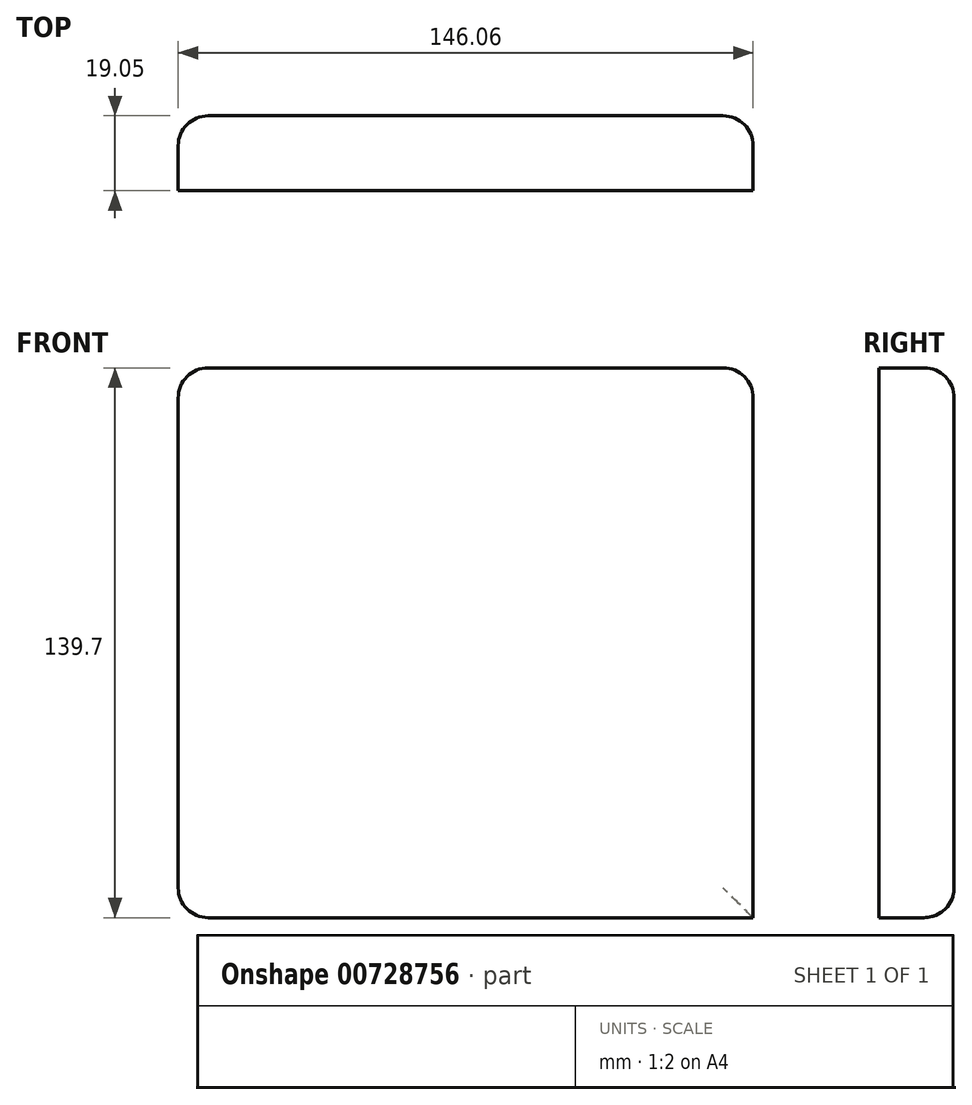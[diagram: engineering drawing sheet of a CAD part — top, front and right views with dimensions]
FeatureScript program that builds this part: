
annotation { "Feature Type Name" : "Feature", "Feature Type Description" : "" }
export const myFeature = defineFeature(function(context is Context, id is Id, definition is map)
    precondition{}
    {
        {
            var Q0;
            Q0=qCreatedBy(makeId("Front.planeOp"),FACE);
            var sketch = newSketch(context, id + "F0", { "sketchPlane" : qUnion([Q0])});
            skLineSegment(sketch, "E0.bottom", {"start": v(73.03, -69.85) * mm, "end": v(-73.03, -69.85) * mm});
            skLineSegment(sketch, "E0.top", {"start": v(73.03, 69.85) * mm, "end": v(-73.03, 69.85) * mm});
            skLineSegment(sketch, "E0.left", {"start": v(73.03, -69.85) * mm, "end": v(73.03, 69.85) * mm});
            skLineSegment(sketch, "E0.right", {"start": v(-73.03, -69.85) * mm, "end": v(-73.03, 69.85) * mm});
            skPoint(sketch, "E0.middle", {"position": v(0, 0) * mm});
            skSolve(sketch);
        }
        {
            var Q0;
            Q0=qSketchRegion(id+"F0",true);
            extrude(context, id + "F1", {"entities" : qUnion([Q0]), "depth" : 19.05 * mm, "offsetDistance" : 25.4 * mm});
        }
        {
            var Q0;
            Q0=makeQuery(id+"F1.opExtrude","CAP_EDGE",EDGE,{"disambiguationData":[OSD([sQuery(id+"F0.wireOp",EDGE,"E0.left")])],"isStart":true});
            var Q1;
            Q1=makeQuery(id+"F1.opExtrude","CAP_EDGE",EDGE,{"disambiguationData":[OSD([sQuery(id+"F0.wireOp",EDGE,"E0.top")])],"isStart":true});
            var Q2;
            Q2=makeQuery(id+"F1.opExtrude","CAP_EDGE",EDGE,{"disambiguationData":[OSD([sQuery(id+"F0.wireOp",EDGE,"E0.right")])],"isStart":true});
            var Q3;
            Q3=makeQuery(id+"F1.opExtrude","CAP_EDGE",EDGE,{"disambiguationData":[OSD([sQuery(id+"F0.wireOp",EDGE,"E0.bottom")])],"isStart":true});
            fillet(context, id + "F2", {"entities" : qUnion([Q0, Q1, Q2, Q3]), "radius" : 7.62 * mm, "tangentPropagation" : true, "allowEdgeOverflow" : false});
        }
        {
            var Q0;
            Q0=makeQuery(id+"F1.opExtrude","SWEPT_EDGE",EDGE,{"disambiguationData":[OSD([sQuery(id+"F0.wireOp",EDGE,"E0.top"),sQuery(id+"F0.wireOp",EDGE,"E0.right")])]});
            var Q1;
            Q1=makeQuery(id+"F1.opExtrude","SWEPT_EDGE",EDGE,{"disambiguationData":[OSD([sQuery(id+"F0.wireOp",EDGE,"E0.top"),sQuery(id+"F0.wireOp",EDGE,"E0.left")])]});
            fillet(context, id + "F3", {"entities" : qUnion([Q0, Q1]), "radius" : 7.62 * mm, "tangentPropagation" : true, "allowEdgeOverflow" : false});
        }
        {
            var Q0;
            Q0=makeQuery(id+"F1.opExtrude","SWEPT_EDGE",EDGE,{"disambiguationData":[OSD([sQuery(id+"F0.wireOp",EDGE,"E0.bottom"),sQuery(id+"F0.wireOp",EDGE,"E0.right")])]});
            fillet(context, id + "F4", {"entities" : qUnion([Q0]), "radius" : 7.62 * mm, "tangentPropagation" : true, "allowEdgeOverflow" : false});
        }
    });
